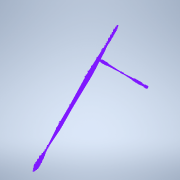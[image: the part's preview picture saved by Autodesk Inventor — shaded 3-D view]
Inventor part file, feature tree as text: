
AUTODESK INVENTOR PART (.ipt)
format: ipt  version: 2021 (Build 250183000, 183)  size: 972,288 bytes
history: native  units: in
note: dims shown in document units (in); Inventor stores cm internally (conversion verified against a paired STEP export)
features: sketch x3, other x1
ambient origin geometry x8: Origin, YZ Plane, XZ Plane, XY Plane, X Axis, Y Axis, Z Axis, Center Point
feature tree (4):
  other  "Repaired Geometry1"
  sketch  "Sketch4"
  sketch  "Sketch5"
  sketch  "3D Sketch1"
